SOLIDWORKS PART (.sldprt)
format: sldprt  version: not decoded by parser v0  size: 101,888 bytes
history: native  units: mm
features: plane x3, sketch x3, material x1, revolve x1, cut_extrude x1, extrude x1, chamfer x1 + 1 further entry (+10 scaffold rows collapsed)
feature tree (22):
  scaffold x10  (default folders/planes/origin — collapsed)
  material  "Matériau <non spécifié>"
  "Corps de surface"
  plane  "Face"
  plane  "Dessus"
  plane  "Droite"
  sketch  "Esquisse1"  dims[c1.D1=2.5mm c1.D2=1.5mm c1.D3=2.0mm c1.D4=10.0mm c1.D7=0.8mm c2.D2=10.0mm c2.D4=1.5mm c3.D2=0.2mm c3.D9=0.2mm]
  revolve  "Révolution1"  Angle=360deg
  sketch  "Esquisse2"  dims[D3=0.2mm D4=0.2mm]
  cut_extrude  "Enlèv. mat.-Extru.1"  Depth=10mm
  sketch  "Esquisse3"  dims[D1=~1.454778mm]
  extrude  "Extrusion1"  Depth=8mm
  chamfer  "Chanfrein1"  Distance=0.3mm Angle=45deg
decode coverage: 7 of 7 modeling features carry decoded parameters; 1 rows unclassified (native names shown)
note: ~ marks probable driven/reference dimensions
note: suppression state not decoded; provenance and decode notes live in map.json
